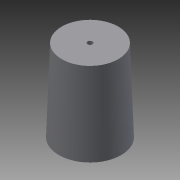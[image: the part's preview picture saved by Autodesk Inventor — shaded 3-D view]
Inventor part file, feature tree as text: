
AUTODESK INVENTOR PART (.ipt)
format: ipt  version: 2013 SP2 (Build 170200200, 200)  size: 95,232 bytes
history: native  units: mm
features: revolve x1
ambient origin geometry x8: Origin, YZ Plane, XZ Plane, XY Plane, X Axis, Y Axis, Z Axis, Center Point
bodies: Solid1 (feature_tree)
feature tree (1):
  revolve  "Revolution1"  [1 undecoded]
note: 1 required parameter value undecoded (feature->parameter linkage not recoverable at this tier; creation-order binding heuristic only, values carry confidence <= 0.55)
